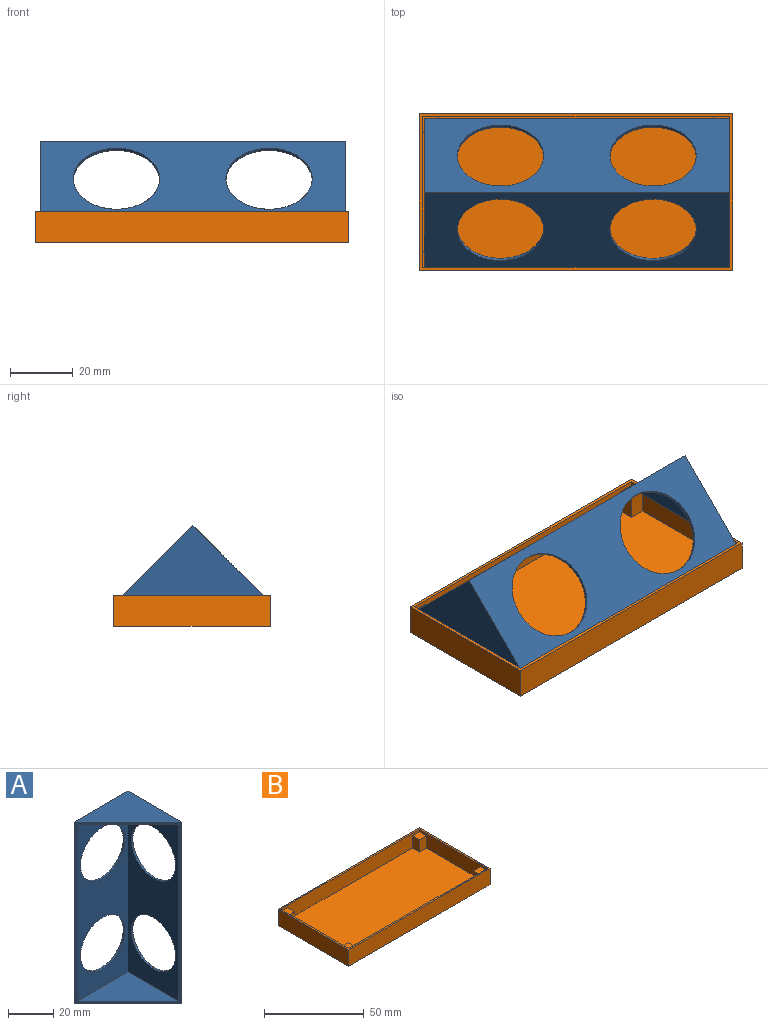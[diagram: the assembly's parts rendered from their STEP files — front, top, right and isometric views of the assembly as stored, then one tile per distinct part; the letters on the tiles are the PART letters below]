
ASSEMBLY  parts=2 mates=1
PART A: 13 faces, bbox 33.6x33.6x97.5 mm
  f0: plane 97.5x33.59mm, normal (-0.71,-0.71,0), area 365.1mm2, adj f1,f2,f3,f4,f5,f6,f7,f8
  f1: plane 97.5x33.59mm, normal (1,0,0), area 2079.3mm2, adj f0,f2,f3,f4,f9,f10
  f2: plane 97.5x33.59mm, normal (0,1,0), area 2079.3mm2, adj f0,f1,f3,f4,f11,f12
  f3: plane 33.59x33.59mm, normal (0,0,1), area 564.1mm2, adj f0,f1,f2
  f4: plane 33.59x33.59mm, normal (0,0,-1), area 564.1mm2, adj f0,f1,f2
  f5: plane 95.5x31.59mm, normal (-1,0,0), area 1821.1mm2, adj f0,f6,f7,f8,f9,f10
  f6: plane 95.5x31.59mm, normal (0,-1,0), area 1821.1mm2, adj f0,f5,f7,f8,f11,f12
  f7: plane 31.59x31.59mm, normal (0,0,-1), area 498.9mm2, adj f0,f5,f6
  f8: plane 31.59x31.59mm, normal (0,0,1), area 498.9mm2, adj f0,f5,f6
  f9: cylinder r=13.79mm len=27.59mm, axis (1,0,0), area 86.7mm2, adj f1,f5
  f10: cylinder r=13.79mm len=27.59mm, axis (1,0,0), area 86.7mm2, adj f1,f5
  f11: cylinder r=13.79mm len=27.59mm, axis (0,1,0), area 86.7mm2, adj f2,f6
  f12: cylinder r=13.79mm len=27.59mm, axis (0,1,0), area 86.7mm2, adj f2,f6
PART B: 23 faces, bbox 100x50x10 mm
  f0: plane 98x48mm, normal (0,0,1), area 4604mm2, adj f1,f2,f9,f10,f12,f13,f15,f16
  f1: plane 98x9mm, normal (0,1,0), area 807mm2, adj f0,f2,f3,f9,f14,f16,f20,f22
  f2: plane 48x9mm, normal (1,0,0), area 357mm2, adj f0,f1,f3,f10,f11,f12,f14,f15
  f3: plane 100x50mm, normal (0,0,1), area 296mm2, adj f1,f2,f4,f5,f6,f7,f9,f10
  f4: plane 100x10mm, normal (0,-1,0), area 1000mm2, adj f3,f5,f7,f8
  f5: plane 50x10mm, normal (1,0,0), area 500mm2, adj f3,f4,f6,f8
  f6: plane 100x10mm, normal (0,1,0), area 1000mm2, adj f3,f5,f7,f8
  f7: plane 50x10mm, normal (-1,0,0), area 500mm2, adj f3,f4,f6,f8
  f8: plane 100x50mm, normal (0,0,-1), area 5000mm2, adj f4,f5,f6,f7
  f9: plane 48x9mm, normal (-1,0,0), area 357mm2, adj f0,f1,f3,f10,f17,f18,f20,f21
  f10: plane 98x9mm, normal (0,-1,0), area 807mm2, adj f0,f2,f3,f9,f11,f13,f17,f19
  f11: plane 5x5mm, normal (0,0,1), area 25mm2, adj f2,f10,f12,f13
  f12: plane 7.5x5mm, normal (0,-1,0), area 37.5mm2, adj f0,f2,f11,f13
  f13: plane 7.5x5mm, normal (1,0,0), area 37.5mm2, adj f0,f10,f11,f12
  f14: plane 5x5mm, normal (0,0,1), area 25mm2, adj f1,f2,f15,f16
  f15: plane 7.5x5mm, normal (0,1,0), area 37.5mm2, adj f0,f2,f14,f16
  f16: plane 7.5x5mm, normal (1,0,0), area 37.5mm2, adj f0,f1,f14,f15
  f17: plane 5x5mm, normal (0,0,1), area 25mm2, adj f9,f10,f18,f19
  f18: plane 7.5x5mm, normal (0,-1,0), area 37.5mm2, adj f0,f9,f17,f19
  f19: plane 7.5x5mm, normal (-1,0,0), area 37.5mm2, adj f0,f10,f17,f18
  f20: plane 5x5mm, normal (0,0,1), area 25mm2, adj f1,f9,f21,f22
  f21: plane 7.5x5mm, normal (0,1,0), area 37.5mm2, adj f0,f9,f20,f22
  f22: plane 7.5x5mm, normal (-1,0,0), area 37.5mm2, adj f0,f1,f20,f21
PLACE A rot(axis=(0.36,-0.86,-0.36),98.4deg) t=(49,-1.5,5)mm
PLACE B t=(0,-1.25,-3.5)mm
MATE fastened A.f0 <-> B.f20  axis (0,0,-1) through (49,-25.25,5)mm
